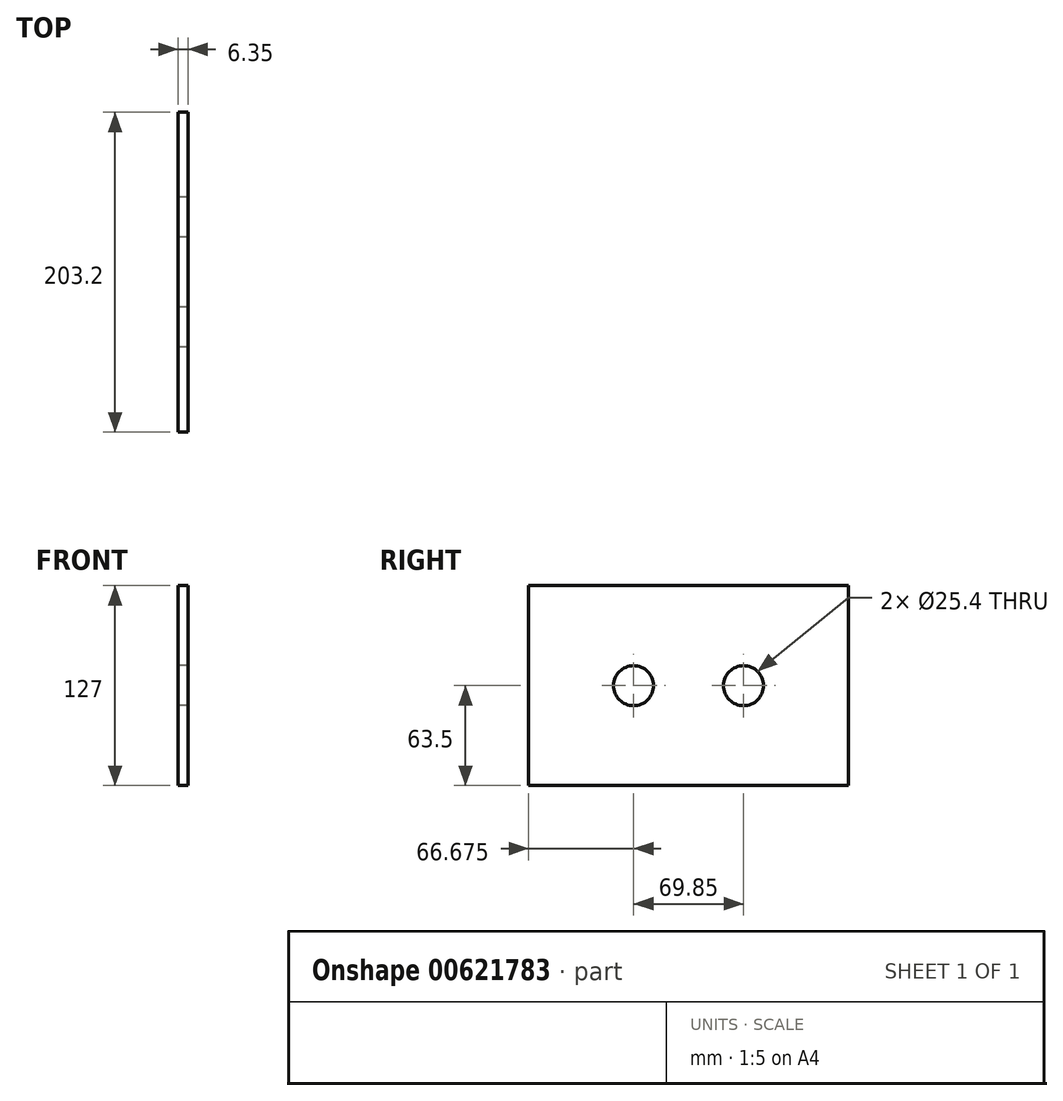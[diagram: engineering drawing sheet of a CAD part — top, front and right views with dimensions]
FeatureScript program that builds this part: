
annotation { "Feature Type Name" : "Feature", "Feature Type Description" : "" }
export const myFeature = defineFeature(function(context is Context, id is Id, definition is map)
    precondition{}
    {
        {
            var Q0;
            Q0=qCreatedBy(makeId("Right.planeOp"),FACE);
            var sketch = newSketch(context, id + "F0", { "sketchPlane" : qUnion([Q0])});
            skLineSegment(sketch, "E0.bottom", {"start": v(101.6, -63.5) * mm, "end": v(-101.6, -63.5) * mm});
            skLineSegment(sketch, "E0.top", {"start": v(101.6, 63.5) * mm, "end": v(-101.6, 63.5) * mm});
            skLineSegment(sketch, "E0.left", {"start": v(101.6, -63.5) * mm, "end": v(101.6, 63.5) * mm});
            skLineSegment(sketch, "E0.right", {"start": v(-101.6, -63.5) * mm, "end": v(-101.6, 63.5) * mm});
            skPoint(sketch, "E0.middle", {"position": v(0, 0) * mm});
            skLineSegment(sketch, "E1", {"start": v(0, 0) * mm, "end": v(-34.93, 0) * mm, "construction": true});
            skLineSegment(sketch, "E2", {"start": v(-34.93, 0) * mm, "end": v(0, 0) * mm, "construction": true});
            skLineSegment(sketch, "E3", {"start": v(0, 0) * mm, "end": v(34.93, 0) * mm, "construction": true});
            skCircle(sketch, "E4", {"center": v(-34.93, 0) * mm, "radius": 12.7 * mm});
            skCircle(sketch, "E5", {"center": v(34.93, 0) * mm, "radius": 12.7 * mm});
            skSolve(sketch);
        }
        {
            var Q0;
            Q0=makeQuery(id+"F0.imprint","IMPRINT",FACE,{"disambiguationData":[TD([[makeQuery(id+"F0.imprint","IMPRINT",EDGE,{"derivedFrom":sQuery(id+"F0.wireOp",EDGE,"E0.bottom")}),-1.0]])]});
            extrude(context, id + "F1", {"entities" : qUnion([Q0]), "depth" : 6.35 * mm, "offsetDistance" : 25.4 * mm});
        }
    });
